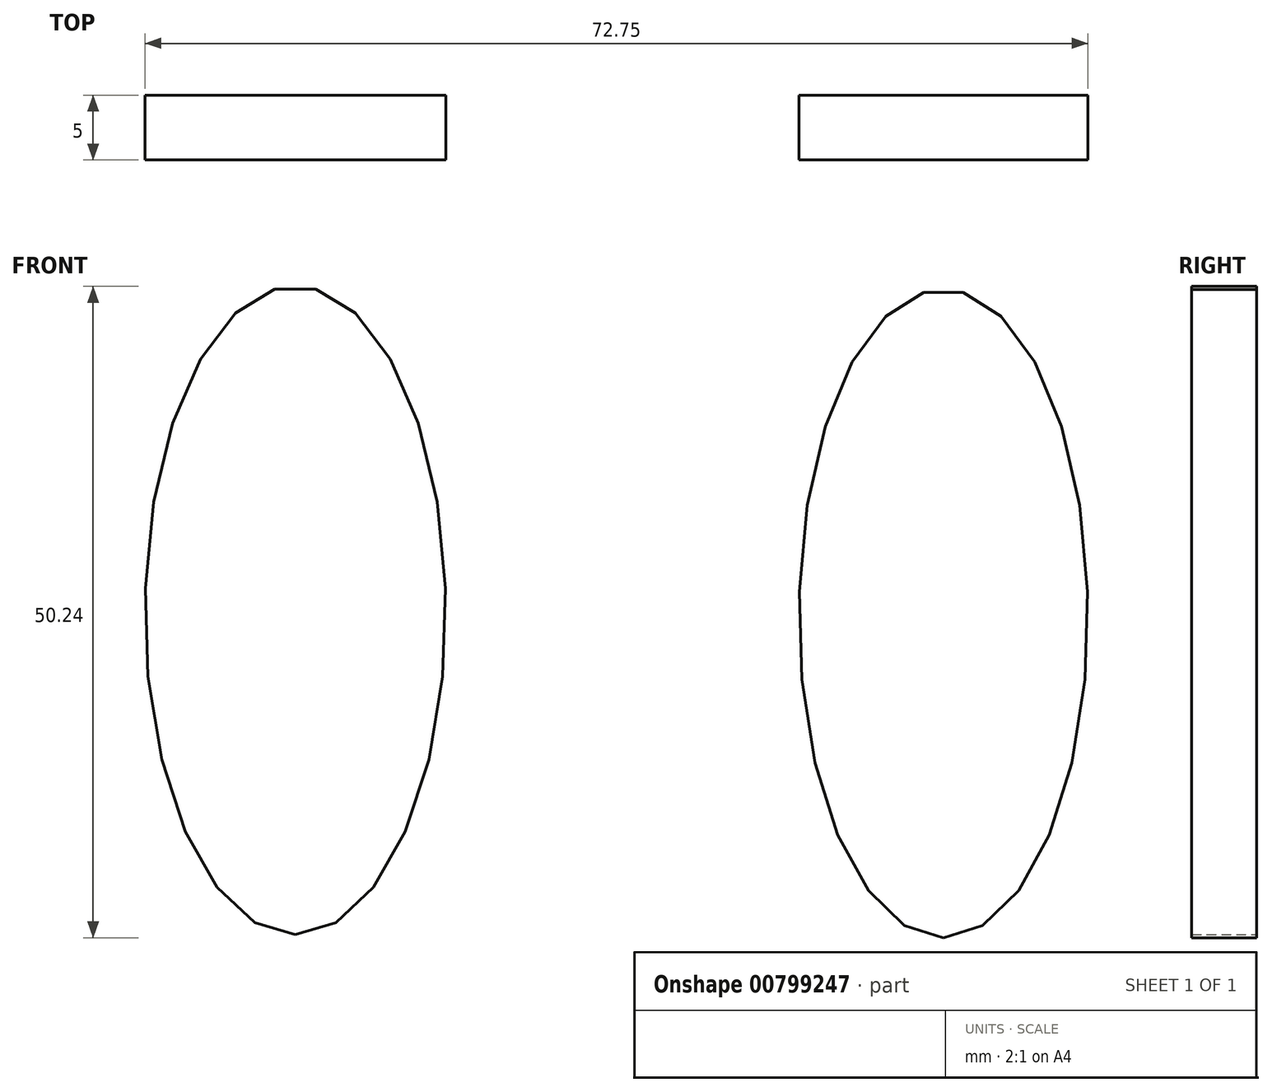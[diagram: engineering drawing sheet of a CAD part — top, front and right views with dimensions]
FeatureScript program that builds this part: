
annotation { "Feature Type Name" : "Feature", "Feature Type Description" : "" }
export const myFeature = defineFeature(function(context is Context, id is Id, definition is map)
    precondition{}
    {
        {
            var Q0;
            Q0=qCreatedBy(makeId("Front.planeOp"),FACE);
            var sketch = newSketch(context, id + "F0", { "sketchPlane" : qUnion([Q0])});
            skEllipse(sketch, "E0", {"center": v(-36.88, -23.63) * mm, "majorRadius": 25 * mm, "minorRadius": 11.6 * mm, "majorAxis": v(0, -1)});
            skEllipse(sketch, "E1", {"center": v(13.12, -23.87) * mm, "majorRadius": 25 * mm, "minorRadius": 11.15 * mm, "majorAxis": v(0, -1)});
            skSolve(sketch);
        }
        {
            var Q0;
            Q0=makeQuery(id+"F0.imprint","IMPRINT",FACE,{"disambiguationData":[TD([[makeQuery(id+"F0.imprint","IMPRINT",EDGE,{"derivedFrom":sQuery(id+"F0.wireOp",EDGE,"E0")}),1.0]])]});
            var Q1;
            Q1=makeQuery(id+"F0.imprint","IMPRINT",FACE,{"disambiguationData":[TD([[makeQuery(id+"F0.imprint","IMPRINT",EDGE,{"derivedFrom":sQuery(id+"F0.wireOp",EDGE,"E1")}),1.0]])]});
            extrude(context, id + "F1", {"entities" : qUnion([Q0, Q1]), "depth" : 5 * mm, "offsetDistance" : 25 * mm});
        }
    });
